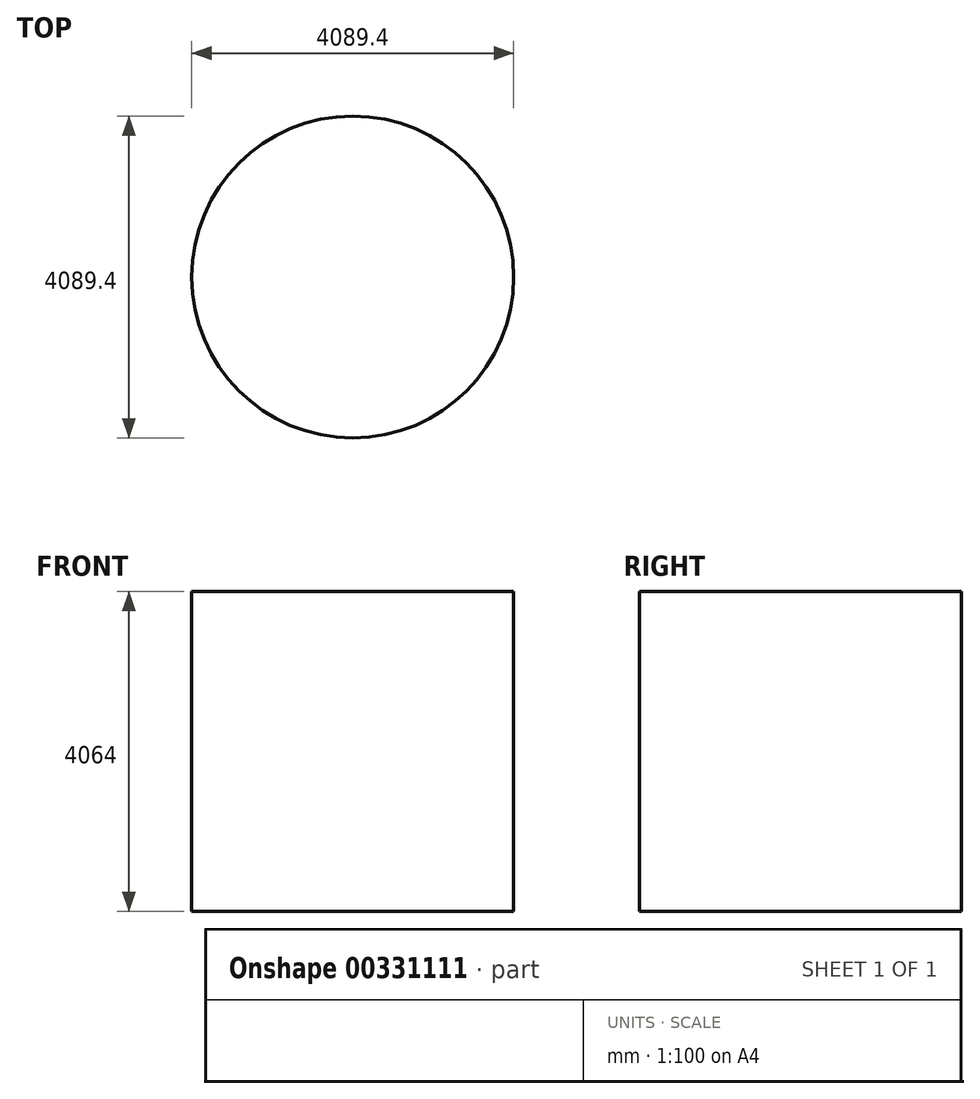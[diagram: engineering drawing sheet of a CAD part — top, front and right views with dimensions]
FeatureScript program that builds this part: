
annotation { "Feature Type Name" : "Feature", "Feature Type Description" : "" }
export const myFeature = defineFeature(function(context is Context, id is Id, definition is map)
    precondition{}
    {
        {
            var Q0;
            Q0=qCreatedBy(makeId("Top.planeOp"),FACE);
            var sketch = newSketch(context, id + "F0", { "sketchPlane" : qUnion([Q0])});
            skCircle(sketch, "E0", {"center": v(0, 0) * mm, "radius": 2044.7 * mm});
            skSolve(sketch);
        }
        {
            var Q0;
            Q0 = qSketchRegion(id + "F0", true);
            extrude(context, id + "F1", {"entities" : qUnion([Q0]), "depth" : 4064 * mm});
        }
    });
